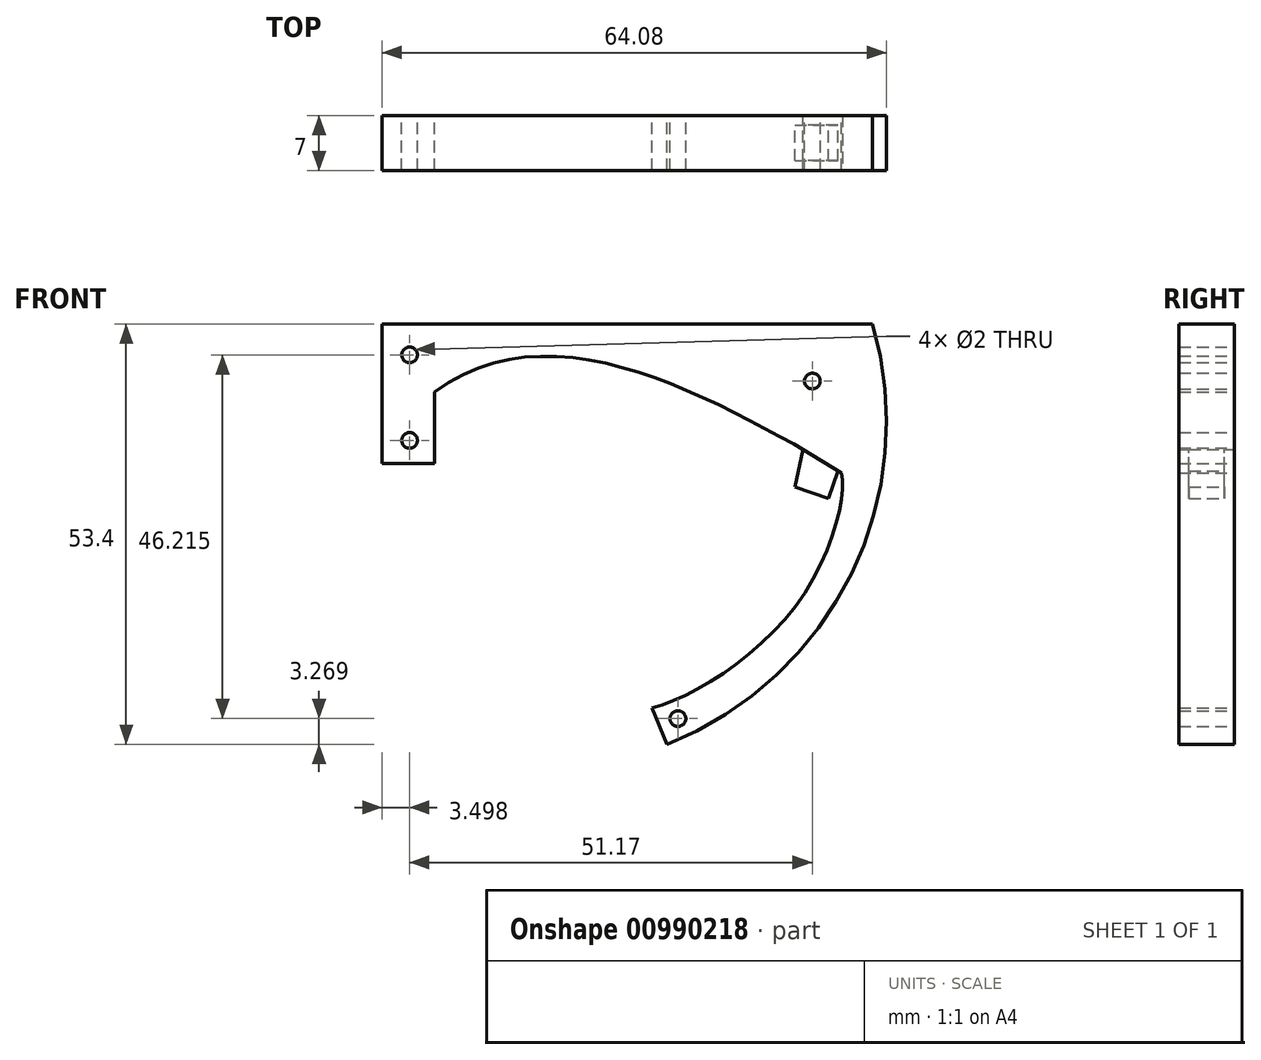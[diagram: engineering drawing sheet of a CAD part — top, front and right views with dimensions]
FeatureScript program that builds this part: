
annotation { "Feature Type Name" : "Feature", "Feature Type Description" : "" }
export const myFeature = defineFeature(function(context is Context, id is Id, definition is map)
    precondition{}
    {
        {
            var Q0;
            Q0=qCreatedBy(makeId("Front.planeOp"),FACE);
            var sketch = newSketch(context, id + "F0", { "sketchPlane" : qUnion([Q0])});
            skLineSegment(sketch, "E0", {"start": v(0, 21.44) * mm, "end": v(62.3, 21.44) * mm});
            skLineSegment(sketch, "E1", {"start": v(34.3, -27.32) * mm, "end": v(36.18, -31.96) * mm});
            skArc(sketch, "E2", {"start": v(36.18, -31.96) * mm, "mid": v(59.6, -10.33) * mm, "end": v(62.3, 21.44) * mm});
            skCircle(sketch, "E3", {"center": v(3.5, 17.52) * mm, "radius": 1 * mm});
            skCircle(sketch, "E4", {"center": v(3.5, 6.66) * mm, "radius": 1 * mm});
            skCircle(sketch, "E5", {"center": v(54.67, 14.2) * mm, "radius": 1 * mm});
            skCircle(sketch, "E6", {"center": v(37.59, -28.7) * mm, "radius": 1 * mm});
            skCircle(sketch, "E7", {"center": v(19.82, 11.13) * mm, "radius": 1 * mm, "construction": true});
            skLineSegment(sketch, "E8", {"start": v(0, 21.44) * mm, "end": v(0, 3.73) * mm});
            skLineSegment(sketch, "E9", {"start": v(6.67, 3.73) * mm, "end": v(6.67, 12.79) * mm});
            skFitSpline(sketch, "E10", {"points": [v(34.3, -27.32) * mm, v(52.88, -13.89) * mm, v(58.33, 2.5) * mm], "startDerivative": vector(28.58, 7.3) * mm, "endDerivative": vector(-4.8, 17.89) * mm});
            skLineSegment(sketch, "E11", {"start": v(58.33, 2.5) * mm, "end": v(53.49, 5.5) * mm});
            skFitSpline(sketch, "E12", {"points": [v(6.67, 12.79) * mm, v(52.3, 6.17) * mm], "startDerivative": vector(41.09, 30.77) * mm, "endDerivative": vector(41.7, -23.1) * mm});
            skLineSegment(sketch, "E13", {"start": v(52.43, 0.74) * mm, "end": v(53.49, 5.5) * mm});
            skLineSegment(sketch, "E14", {"start": v(0, 0) * mm, "end": v(0, 3.73) * mm, "construction": true});
            skLineSegment(sketch, "E15", {"start": v(36.33, -26.67) * mm, "end": v(36.26, -26.54) * mm, "construction": true});
            skLineSegment(sketch, "E16", {"start": v(36.26, -26.54) * mm, "end": v(9.74, -26.9) * mm, "construction": true});
            skFitSpline(sketch, "E17", {"points": [v(7, 3.73) * mm, v(29.13, 3.73) * mm], "startDerivative": vector(31, 59.2) * mm, "endDerivative": vector(6.79, -24.68) * mm, "construction": true});
            skFitSpline(sketch, "E18", {"points": [v(38.66, -22.42) * mm, v(36.26, -26.54) * mm], "startDerivative": vector(0.1, -0.88) * mm, "endDerivative": vector(-2.4, -0.14) * mm, "construction": true});
            skLineSegment(sketch, "E19", {"start": v(38.66, -22.42) * mm, "end": v(40.62, -20.92) * mm, "construction": true});
            skLineSegment(sketch, "E20", {"start": v(40.62, -20.92) * mm, "end": v(38.56, -16.92) * mm, "construction": true});
            skLineSegment(sketch, "E21", {"start": v(38.56, -16.92) * mm, "end": v(36.96, -17.74) * mm, "construction": true});
            skLineSegment(sketch, "E22", {"start": v(39.59, -18.92) * mm, "end": v(37.73, -19.87) * mm, "construction": true});
            skLineSegment(sketch, "E23", {"start": v(197.2, -24.34) * mm, "end": v(197.2, -21.9) * mm, "construction": true});
            skLineSegment(sketch, "E24", {"start": v(34.44, -21.9) * mm, "end": v(32.2, -21.9) * mm, "construction": true});
            skLineSegment(sketch, "E25", {"start": v(17.97, -26.78) * mm, "end": v(17.97, -26.79) * mm, "construction": true});
            skLineSegment(sketch, "E26", {"start": v(52.3, 6.17) * mm, "end": v(53.49, 5.5) * mm});
            skLineSegment(sketch, "E27", {"start": v(0, 3.73) * mm, "end": v(6.67, 3.73) * mm});
            skLineSegment(sketch, "E28", {"start": v(52.43, 0.74) * mm, "end": v(56.68, -0.74) * mm});
            skLineSegment(sketch, "E29", {"start": v(56.68, -0.74) * mm, "end": v(57.9, 2.76) * mm});
            skSolve(sketch);
        }
        {
            var Q0;
            Q0=makeQuery(id+"F0.imprint","IMPRINT",FACE,{"disambiguationData":[TD([[makeQuery(id+"F0.imprint","IMPRINT",EDGE,{"derivedFrom":sQuery(id+"F0.wireOp",EDGE,"E0")}),-1.0]])]});
            extrude(context, id + "F1", {"entities" : qUnion([Q0]), "endBound" : BoundingType.SYMMETRIC, "depth" : 7 * mm, "offsetDistance" : 25 * mm});
        }
        {
            var Q0;
            {var subQ0=sQuery(id+"F0.wireOp",EDGE,"E13");Q0=makeQuery(id+"F0.imprint","IMPRINT",FACE,{"disambiguationData":[TD([[makeQuery(id+"F0.imprint","IMPRINT",EDGE,{"derivedFrom":subQ0}),-1.0]])]});}
            var Q1;
            {var subQ0=sQuery(id+"F0.wireOp",EDGE,"nWu9F3C5-wLr1-OKcC-3tod-9i7FgU31WUD7");Q1=makeQuery(id+"F0.imprint","IMPRINT",FACE,{"disambiguationData":[TD([[makeQuery(id+"F0.imprint","IMPRINT",EDGE,{"derivedFrom":subQ0}),1.0]])]});}
            extrude(context, id + "F2", {"entities" : qUnion([Q0, Q1]), "operationType" : NewBodyOperationType.ADD, "endBound" : BoundingType.SYMMETRIC, "depth" : 4.5 * mm, "offsetDistance" : 25 * mm});
        }
    });
